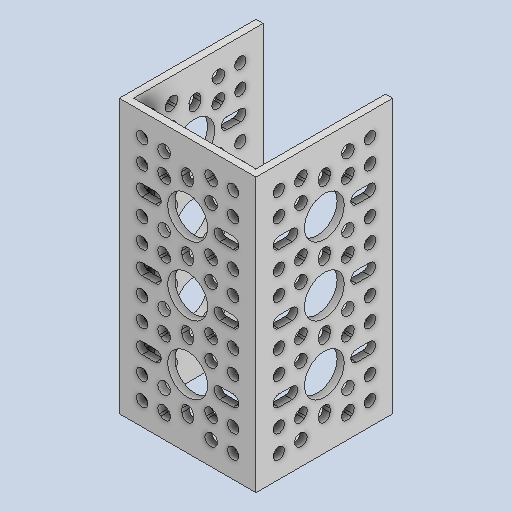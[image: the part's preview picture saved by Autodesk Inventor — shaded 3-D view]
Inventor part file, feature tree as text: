
AUTODESK INVENTOR PART (.ipt)
format: ipt  version: 2022 (Build 260153000, 153)  size: 556,032 bytes
history: native  units: in
note: dims shown in document units (in); Inventor stores cm internally (conversion verified against a paired STEP export)
features: mirror x1
ambient origin geometry x8: Origin, YZ Plane, XZ Plane, XY Plane, X Axis, Y Axis, Z Axis, Center Point
bodies: Solid1 (feature_tree)
feature tree (1):
  mirror  "Mirror7"
